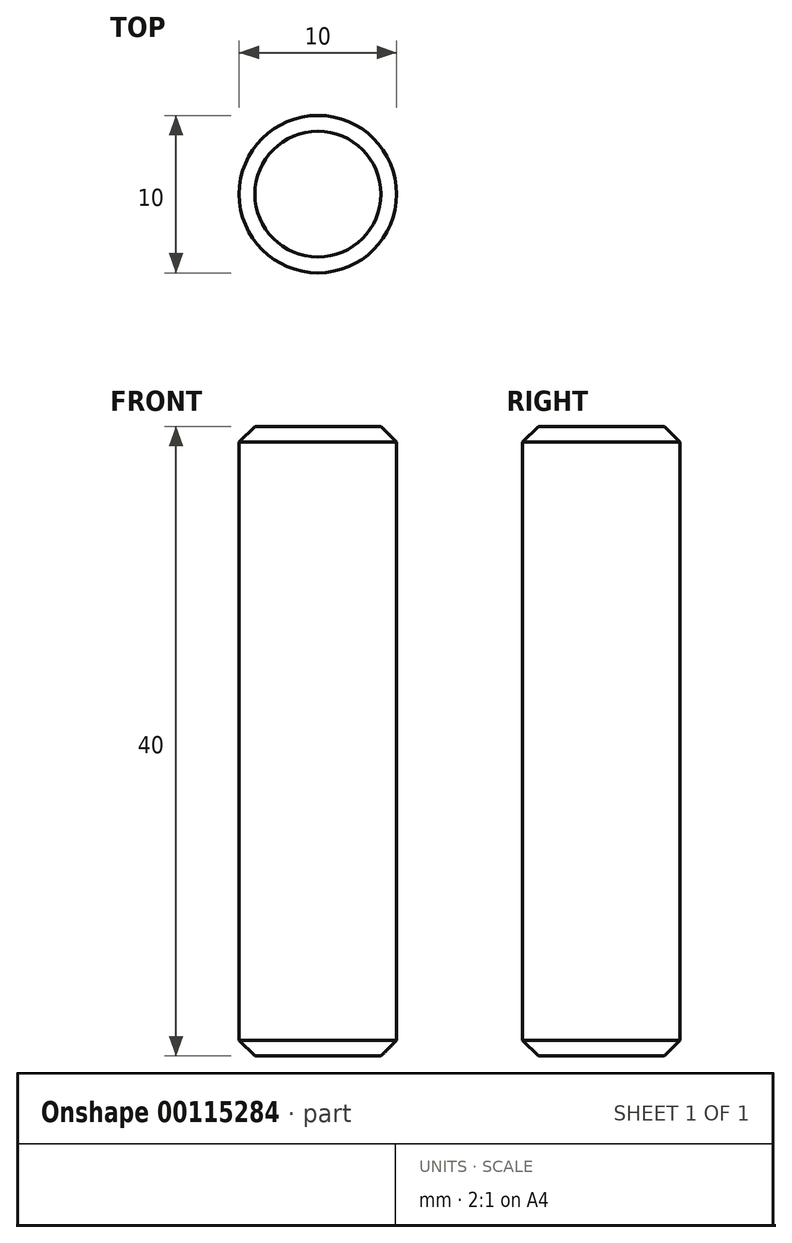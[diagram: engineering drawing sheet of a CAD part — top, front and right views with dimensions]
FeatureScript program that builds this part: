
annotation { "Feature Type Name" : "Feature", "Feature Type Description" : "" }
export const myFeature = defineFeature(function(context is Context, id is Id, definition is map)
    precondition{}
    {
        {
            var Q0;
            Q0=qCreatedBy(makeId("Top.planeOp"),FACE);
            var sketch = newSketch(context, id + "F0", { "sketchPlane" : qUnion([Q0])});
            skCircle(sketch, "E0", {"center": v(252.21, -177.8) * mm, "radius": 5 * mm});
            skSolve(sketch);
        }
        {
            var Q0;
            Q0=qSketchRegion(id+"F0",true);
            extrude(context, id + "F1", {"entities" : qUnion([Q0]), "depth" : 40 * mm});
        }
        {
            var Q0;
            Q0=makeQuery(id+"F8deoI0ds9OQQvR_1.opExtrude","CAP_EDGE",EDGE,{"disambiguationData":[OSD([sQuery(id+"FNSmDNgICrr5992_1.wireOp",EDGE,"WrhgqPip-Hxug-TX0C-coz8-qmcBmcraZFxG")])],"isStart":false});
            var Q1;
            {var subQ0=sQuery(id+"FNSmDNgICrr5992_1.wireOp",EDGE,"QBF4ybXC-I8lF-9HyA-q2n1-7PO9bMuNv2Xd");var subQ1=makeQuery(id+"FOaXZToMlUD9SUw_1.opExtrude","CAP_EDGE",EDGE,{"disambiguationData":[OSD([subQ0])],"isStart":false});Q1=makeQuery(id+"F1XH75m9Bu4Q1Kw_1.opFillet","BLEND_EDGE",EDGE,{"blendedFrom":[makeQuery(id+"F3adTf6APA5g0nj_2.opBoolean","MERGE",EDGE,{"derivedFrom":[subQ1,makeQuery(id+"FOHSBbMP8IG0Sfg_2.opPattern","COPY",EDGE,{"derivedFrom":subQ1,"instanceName":"1"}),makeQuery(id+"FOHSBbMP8IG0Sfg_2.opPattern","COPY",EDGE,{"derivedFrom":subQ1,"instanceName":"2"}),makeQuery(id+"FOHSBbMP8IG0Sfg_2.opPattern","COPY",EDGE,{"derivedFrom":subQ1,"instanceName":"3"}),makeQuery(id+"FOHSBbMP8IG0Sfg_2.opPattern","COPY",EDGE,{"derivedFrom":subQ1,"instanceName":"4"}),makeQuery(id+"FOHSBbMP8IG0Sfg_2.opPattern","COPY",EDGE,{"derivedFrom":subQ1,"instanceName":"5"})]}),makeQuery(id+"F8deoI0ds9OQQvR_1.opExtrude","CAP_FACE",FACE,{"disambiguationData":[OSD([sQuery(id+"FNSmDNgICrr5992_1.wireOp",EDGE,"WrhgqPip-Hxug-TX0C-coz8-qmcBmcraZFxG"),subQ0])],"isStart":false})],"blendedInto":[makeQuery(id+"F8deoI0ds9OQQvR_1.opExtrude","CAP_FACE",FACE,{"disambiguationData":[OSD([sQuery(id+"FNSmDNgICrr5992_1.wireOp",EDGE,"WrhgqPip-Hxug-TX0C-coz8-qmcBmcraZFxG"),subQ0])],"isStart":false})]});}
            var Q2;
            Q2=makeQuery(id+"F5Nv93303G39r8I_3.opExtrude","CAP_EDGE",EDGE,{"disambiguationData":[OSD([sQuery(id+"FpatWay3Y1nzrsI_2.wireOp",EDGE,"FyXStOlr-4eru-C9Gf-DU6Q-nSZis50Lsmzc")])],"isStart":false});
            var Q3;
            {var subQ0=sQuery(id+"FpatWay3Y1nzrsI_2.wireOp",EDGE,"V4fqaZMG-WK9z-iNdc-dBwx-bLhpO43WXJdH");var subQ1=makeQuery(id+"FIPxoUkmKFCymNP_2.opExtrude","CAP_EDGE",EDGE,{"disambiguationData":[OSD([subQ0])],"isStart":false});Q3=makeQuery(id+"FOxRyz4zF4mRUTp_2.opFillet","BLEND_EDGE",EDGE,{"blendedFrom":[makeQuery(id+"FnNP1aSXQnMZEpo_4.opBoolean","MERGE",EDGE,{"derivedFrom":[subQ1,makeQuery(id+"FjADqP8Pk50ClZA_3.opPattern","COPY",EDGE,{"derivedFrom":subQ1,"instanceName":"1"}),makeQuery(id+"FjADqP8Pk50ClZA_3.opPattern","COPY",EDGE,{"derivedFrom":subQ1,"instanceName":"2"}),makeQuery(id+"FjADqP8Pk50ClZA_3.opPattern","COPY",EDGE,{"derivedFrom":subQ1,"instanceName":"3"}),makeQuery(id+"FjADqP8Pk50ClZA_3.opPattern","COPY",EDGE,{"derivedFrom":subQ1,"instanceName":"4"}),makeQuery(id+"FjADqP8Pk50ClZA_3.opPattern","COPY",EDGE,{"derivedFrom":subQ1,"instanceName":"5"})]}),makeQuery(id+"F5Nv93303G39r8I_3.opExtrude","CAP_FACE",FACE,{"disambiguationData":[OSD([sQuery(id+"FpatWay3Y1nzrsI_2.wireOp",EDGE,"FyXStOlr-4eru-C9Gf-DU6Q-nSZis50Lsmzc"),subQ0])],"isStart":false})],"blendedInto":[makeQuery(id+"F5Nv93303G39r8I_3.opExtrude","CAP_FACE",FACE,{"disambiguationData":[OSD([sQuery(id+"FpatWay3Y1nzrsI_2.wireOp",EDGE,"FyXStOlr-4eru-C9Gf-DU6Q-nSZis50Lsmzc"),subQ0])],"isStart":false})]});}
            var Q4;
            Q4=makeQuery(id+"F1.opExtrude","CAP_EDGE",EDGE,{"disambiguationData":[OSD([sQuery(id+"F0.wireOp",EDGE,"E0")])],"isStart":false});
            var Q5;
            Q5=makeQuery(id+"F1.opExtrude","CAP_EDGE",EDGE,{"disambiguationData":[OSD([sQuery(id+"F0.wireOp",EDGE,"E0")])],"isStart":true});
            chamfer(context, id + "F2", {"entities" : qUnion([Q0, Q1, Q2, Q3, Q4, Q5]), "width" : 1 * mm, "tangentPropagation" : true});
        }
    });
